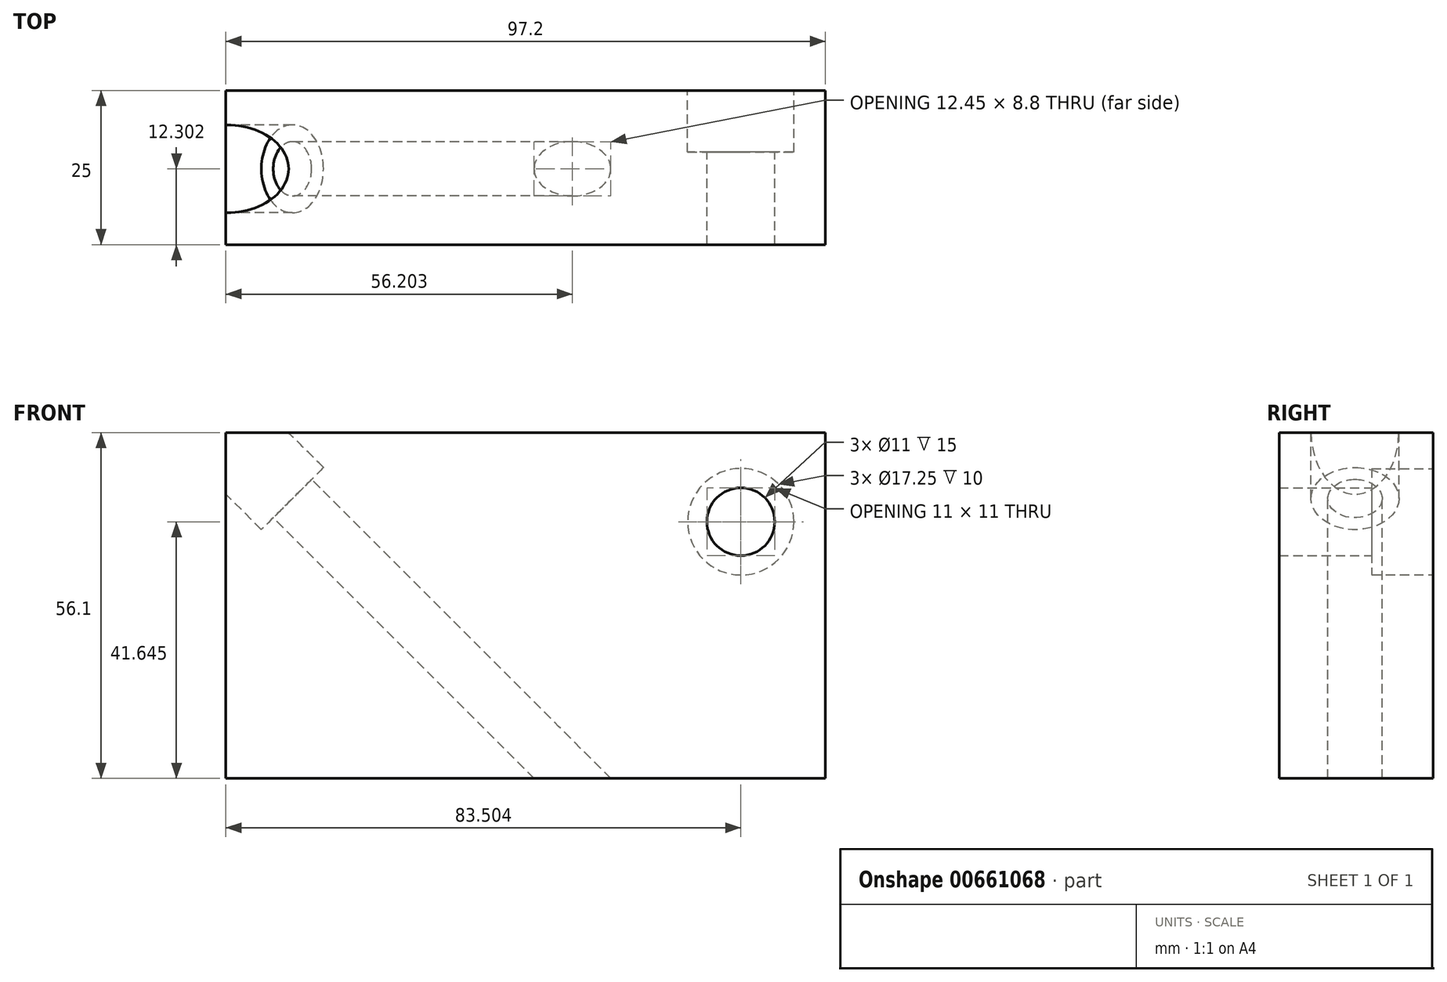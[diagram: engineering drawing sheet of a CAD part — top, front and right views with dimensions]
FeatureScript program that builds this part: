
annotation { "Feature Type Name" : "Feature", "Feature Type Description" : "" }
export const myFeature = defineFeature(function(context is Context, id is Id, definition is map)
    precondition{}
    {
        {
            var Q0;
            Q0=qCreatedBy(makeId("Front.planeOp"),FACE);
            var sketch = newSketch(context, id + "F0", { "sketchPlane" : qUnion([Q0])});
            skLineSegment(sketch, "E0.bottom", {"start": v(-52.65, 32.1) * mm, "end": v(44.55, 32.1) * mm});
            skLineSegment(sketch, "E0.top", {"start": v(-52.65, -24) * mm, "end": v(44.55, -24) * mm});
            skLineSegment(sketch, "E0.left", {"start": v(-52.65, 32.1) * mm, "end": v(-52.65, -24) * mm});
            skLineSegment(sketch, "E0.right", {"start": v(44.55, 32.1) * mm, "end": v(44.55, -24) * mm});
            skPoint(sketch, "E1", {"position": v(-37.44, 19.95) * mm});
            skPoint(sketch, "E2", {"position": v(20.1, 13.27) * mm});
            skSolve(sketch);
        }
        {
            var Q0;
            Q0 = qSketchRegion(id + "F0", true);
            extrude(context, id + "F1", {"entities" : qUnion([Q0]), "depth" : 25 * mm, "offsetDistance" : 25 * mm});
        }
        {
            var Q0;
            Q0=makeQuery(id+"F1.opExtrude","SWEPT_EDGE",EDGE,{"disambiguationData":[OSD([sQuery(id+"F0.wireOp",EDGE,"E0.bottom"),sQuery(id+"F0.wireOp",EDGE,"E0.left")])]});
            cPlane(context, id + "F2", {"entities" : qUnion([Q0]), "cplaneType" : CPlaneType.LINE_ANGLE, "offset" : 25 * mm, "angle" : 135 * degree, "width" : 150 * mm, "height" : 150 * mm});
        }
        {
            var Q0;
            Q0=qCreatedBy(id+"F2.planeOp",FACE);
            var sketch = newSketch(context, id + "F3", { "sketchPlane" : qUnion([Q0])});
            skPoint(sketch, "E3", {"position": v(-12.7, -14.46) * mm});
            skPoint(sketch, "E4", {"position": v(238.1, 113.37) * mm});
            skSolve(sketch);
        }
        {
            var Q0;
            Q0=makeQuery(id+"F1.opExtrude","CAP_FACE",FACE,{"disambiguationData":[OSD([sQuery(id+"F0.wireOp",EDGE,"E0.bottom"),sQuery(id+"F0.wireOp",EDGE,"E0.top"),sQuery(id+"F0.wireOp",EDGE,"E0.left"),sQuery(id+"F0.wireOp",EDGE,"E0.right")])],"isStart":true});
            var sketch = newSketch(context, id + "F4", { "sketchPlane" : qUnion([Q0])});
            skPoint(sketch, "E5", {"position": v(-30.85, 17.64) * mm});
            skSolve(sketch);
        }
        {
            var Q0;
            Q0=sQuery(id+"F4.wireOp",VERTEX,"E5");
            var Q1;
            Q1=makeQuery(id+"F1.opExtrude","SWEPT_BODY",BODY,{"disambiguationData":[OSD([sQuery(id+"F0.wireOp",EDGE,"E0.bottom"),sQuery(id+"F0.wireOp",EDGE,"E0.top"),sQuery(id+"F0.wireOp",EDGE,"E0.left"),sQuery(id+"F0.wireOp",EDGE,"E0.right")])]});
            hole(context, id + "F5", {"style" : HoleStyle.C_BORE, "endStyle" : HoleEndStyle.THROUGH, "standardTappedOrClearance" : lookupTablePath({ "standard" : "ISO", "fit" : "Normal", "size" : "M10", "type" : "Clearance" }), "standardBlindInLast" : lookupTablePath({ "fit" : "Standard", "standard" : "ISO", "size" : "M10", "type" : "Clearance" }), "holeDiameter" : 11 * mm, "cBoreDiameter" : 17.25 * mm, "cBoreDepth" : 10 * mm, "majorDiameter" : 5 * mm, "isTappedThrough" : true, "tappedDepth" : 12 * mm, "tapClearance" : 3, "locations" : qUnion([Q0]), "scope" : qUnion([Q1])});
        }
        {
            var Q0;
            Q0=sQuery(id+"F3.wireOp",VERTEX,"E3");
            var Q1;
            Q1=makeQuery(id+"F1.opExtrude","SWEPT_BODY",BODY,{"disambiguationData":[OSD([sQuery(id+"F0.wireOp",EDGE,"E0.bottom"),sQuery(id+"F0.wireOp",EDGE,"E0.top"),sQuery(id+"F0.wireOp",EDGE,"E0.left"),sQuery(id+"F0.wireOp",EDGE,"E0.right")])]});
            hole(context, id + "F6", {"style" : HoleStyle.C_BORE, "endStyle" : HoleEndStyle.THROUGH, "oppositeDirection" : true, "standardTappedOrClearance" : lookupTablePath({ "standard" : "ISO", "fit" : "Normal", "size" : "M8", "type" : "Clearance" }), "standardBlindInLast" : lookupTablePath({ "fit" : "Standard", "standard" : "ISO", "size" : "M8", "type" : "Clearance" }), "holeDiameter" : 8.8 * mm, "cBoreDiameter" : 14.25 * mm, "cBoreDepth" : 8 * mm, "majorDiameter" : 5 * mm, "isTappedThrough" : true, "tappedDepth" : 12 * mm, "tapClearance" : 3, "locations" : qUnion([Q0]), "scope" : qUnion([Q1])});
        }
    });
